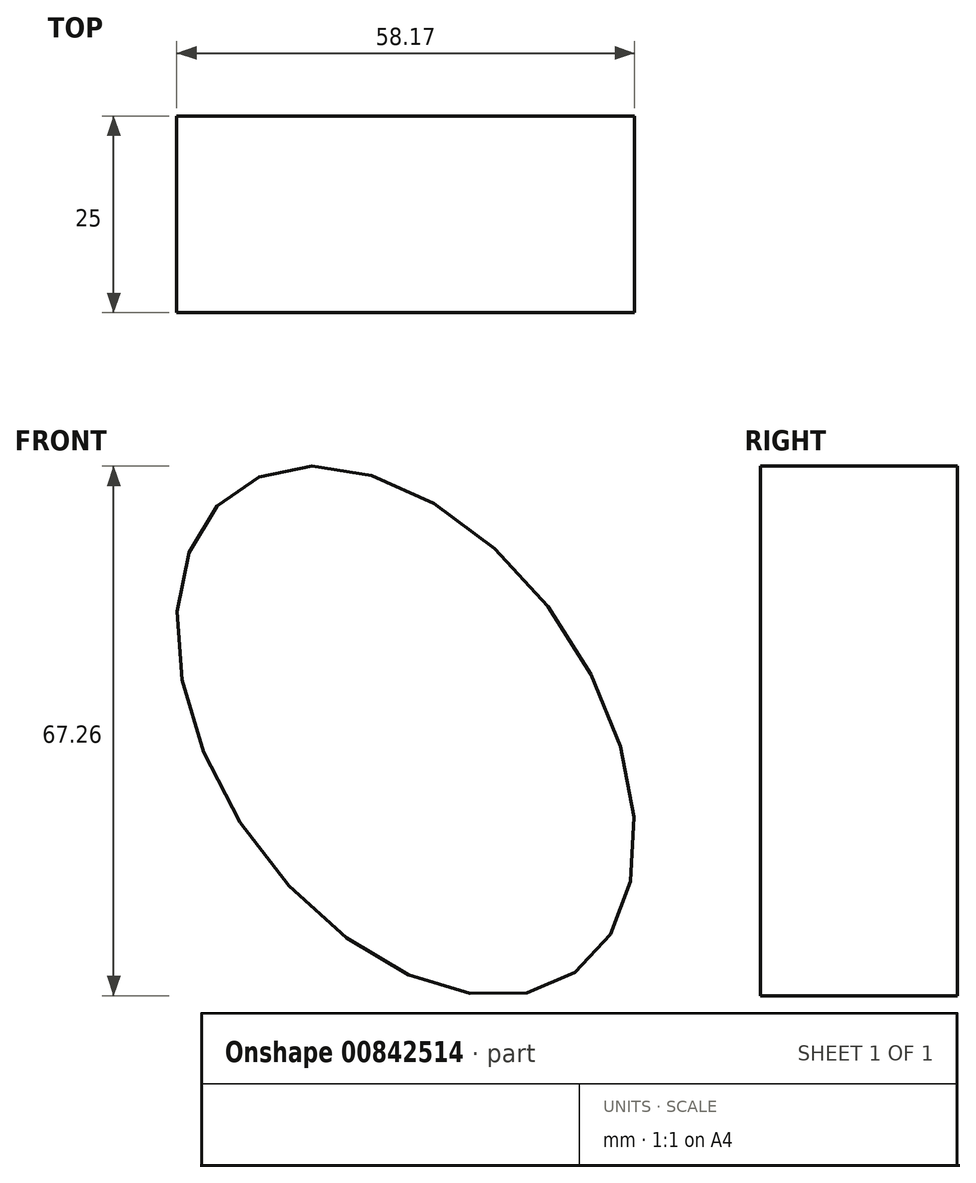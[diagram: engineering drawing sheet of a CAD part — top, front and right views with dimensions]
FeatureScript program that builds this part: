
annotation { "Feature Type Name" : "Feature", "Feature Type Description" : "" }
export const myFeature = defineFeature(function(context is Context, id is Id, definition is map)
    precondition{}
    {
        {
            var Q0;
            Q0=qCreatedBy(makeId("Front.planeOp"),FACE);
            var sketch = newSketch(context, id + "F0", { "sketchPlane" : qUnion([Q0])});
            skLineSegment(sketch, "E0.bottom", {"start": v(0, 0) * mm, "end": v(-181.98, 0) * mm});
            skLineSegment(sketch, "E0.top", {"start": v(0, 114.38) * mm, "end": v(-181.98, 114.38) * mm});
            skLineSegment(sketch, "E0.left", {"start": v(0, 0) * mm, "end": v(0, 114.38) * mm});
            skLineSegment(sketch, "E0.right", {"start": v(-181.98, 0) * mm, "end": v(-181.98, 114.38) * mm});
            skCircle(sketch, "E1", {"center": v(-131.98, 104.38) * mm, "radius": 10 * mm});
            skLineSegment(sketch, "E2", {"start": v(44.4, 22.7) * mm, "end": v(0, 0) * mm});
            skLineSegment(sketch, "E3", {"start": v(-19.09, 128.77) * mm, "end": v(21.56, 157.64) * mm});
            skCircle(sketch, "E4", {"center": v(1.24, 143.2) * mm, "radius": 26.48 * mm});
            skEllipse(sketch, "E5", {"center": v(-305.4, 136.8) * mm, "majorRadius": 37.48 * mm, "minorRadius": 23.92 * mm, "majorAxis": v(0.57, -0.82)});
            skLineSegment(sketch, "E6", {"start": v(-326.9, 167.5) * mm, "end": v(-283.91, 106.1) * mm, "construction": true});
            skSolve(sketch);
        }
        {
            var Q0;
            Q0=makeQuery(id+"F0.imprint","IMPRINT",FACE,{"disambiguationData":[TD([[makeQuery(id+"F0.imprint","IMPRINT",EDGE,{"derivedFrom":sQuery(id+"F0.wireOp",EDGE,"E5")}),1.0]])]});
            extrude(context, id + "F1", {"entities" : qUnion([Q0]), "depth" : 25 * mm, "offsetDistance" : 25 * mm});
        }
    });
